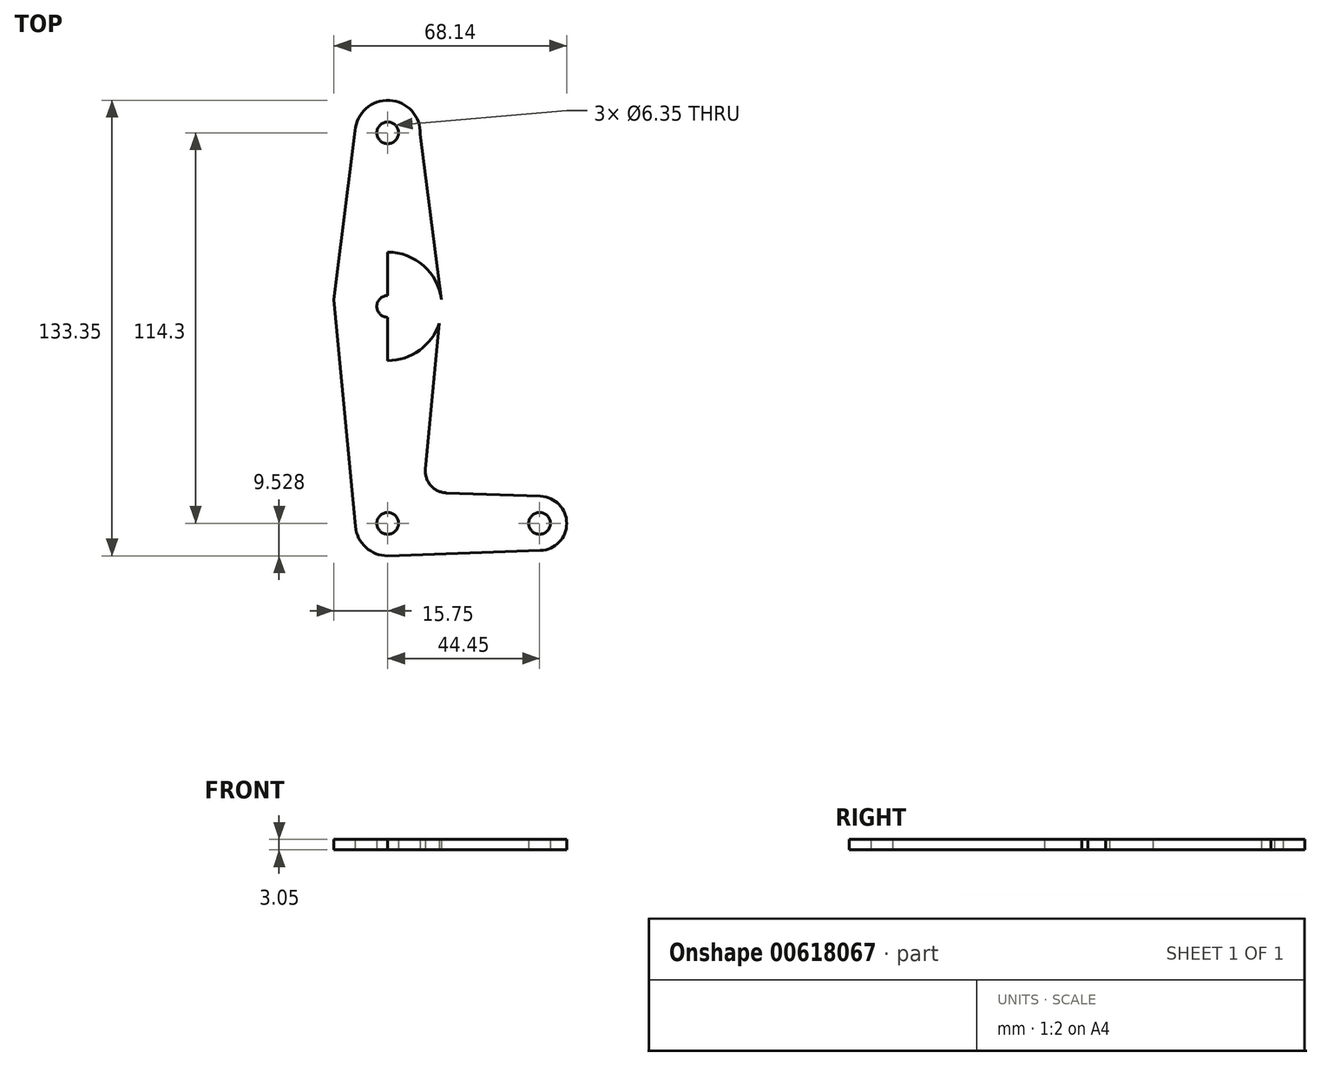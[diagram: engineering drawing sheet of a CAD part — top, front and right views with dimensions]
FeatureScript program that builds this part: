
annotation { "Feature Type Name" : "Feature", "Feature Type Description" : "" }
export const myFeature = defineFeature(function(context is Context, id is Id, definition is map)
    precondition{}
    {
        {
            var Q0;
            Q0=qCreatedBy(makeId("Top.planeOp"),FACE);
            var sketch = newSketch(context, id + "F0", { "sketchPlane" : qUnion([Q0])});
            skLineSegment(sketch, "E0", {"start": v(0, 86.7) * mm, "end": v(0, -27.6) * mm});
            skLineSegment(sketch, "E1", {"start": v(0, -27.6) * mm, "end": v(44.45, -27.6) * mm});
            skCircle(sketch, "E2", {"center": v(0, 86.7) * mm, "radius": 9.53 * mm});
            skCircle(sketch, "E3", {"center": v(0, 35.9) * mm, "radius": 15.88 * mm});
            skCircle(sketch, "E4", {"center": v(0, -27.6) * mm, "radius": 9.53 * mm});
            skCircle(sketch, "E5", {"center": v(44.45, -27.6) * mm, "radius": 7.94 * mm});
            skLineSegment(sketch, "E6", {"start": v(9.52, 86.33) * mm, "end": v(15.75, 37.93) * mm});
            skLineSegment(sketch, "E7", {"start": v(15.75, 37.93) * mm, "end": v(11.06, -11.74) * mm});
            skLineSegment(sketch, "E8", {"start": v(-9.5, 87.31) * mm, "end": v(-15.75, 37.9) * mm});
            skLineSegment(sketch, "E9", {"start": v(-15.75, 37.9) * mm, "end": v(-9.48, -28.49) * mm});
            skLineSegment(sketch, "E10", {"start": v(17.16, -18.68) * mm, "end": v(44.73, -19.66) * mm});
            skLineSegment(sketch, "E11", {"start": v(0, -37.12) * mm, "end": v(44.73, -35.52) * mm});
            skArc(sketch, "E12.filletArc", {"start": v(11.06, -11.74) * mm, "mid": v(12.61, -16.52) * mm, "end": v(17.16, -18.68) * mm});
            skCircle(sketch, "E13", {"center": v(0, 86.7) * mm, "radius": 3.18 * mm});
            skCircle(sketch, "E14", {"center": v(0, 35.9) * mm, "radius": 3.18 * mm});
            skCircle(sketch, "E15", {"center": v(0, -27.6) * mm, "radius": 3.18 * mm});
            skCircle(sketch, "E16", {"center": v(44.45, -27.6) * mm, "radius": 3.18 * mm});
            skSolve(sketch);
        }
        {
            var Q0;
            {var subQ5=sQuery(id+"F0.wireOp",EDGE,"E8");Q0=makeQuery(id+"F0.imprint","IMPRINT",FACE,{"disambiguationData":[TD([[makeQuery(id+"F0.imprint","IMPRINT",EDGE,{"derivedFrom":subQ5}),1.0]])]});}
            var Q1;
            {var subQ5=sQuery(id+"F0.wireOp",EDGE,"E6");Q1=makeQuery(id+"F0.imprint","IMPRINT",FACE,{"disambiguationData":[TD([[makeQuery(id+"F0.imprint","IMPRINT",EDGE,{"derivedFrom":subQ5}),-1.0]])]});}
            var Q2;
            {var subQ0=sQuery(id+"F0.wireOp",EDGE,"E3");var subQ1=sQuery(id+"F0.wireOp",EDGE,"E0");var subQ2=makeQuery(id+"F0.imprint","INTERSECT",VERTEX,{"disambiguationData":[OD(1.0)],"derivedFrom":[subQ1,subQ0]});Q2=makeQuery(id+"F0.imprint","IMPRINT",FACE,{"disambiguationData":[TD([[makeQuery(id+"F0.imprint","IMPRINT",EDGE,{"disambiguationData":[TD([[subQ2,-1.0]])],"derivedFrom":subQ1}),-1.0]])]});}
            var Q3;
            {var subQ11=sQuery(id+"F0.wireOp",EDGE,"E10");Q3=makeQuery(id+"F0.imprint","IMPRINT",FACE,{"disambiguationData":[TD([[makeQuery(id+"F0.imprint","IMPRINT",EDGE,{"derivedFrom":subQ11}),-1.0]])]});}
            var Q4;
            {var subQ0=sQuery(id+"F0.wireOp",EDGE,"E5");var subQ1=sQuery(id+"F0.wireOp",EDGE,"E1");var subQ2=makeQuery(id+"F0.imprint","INTERSECT",VERTEX,{"derivedFrom":[subQ1,subQ0]});Q4=makeQuery(id+"F0.imprint","IMPRINT",FACE,{"disambiguationData":[TD([[makeQuery(id+"F0.imprint","IMPRINT",EDGE,{"disambiguationData":[TD([[subQ2,1.0]])],"derivedFrom":subQ1}),-1.0]])]});}
            var Q5;
            {var subQ1=sQuery(id+"F0.wireOp",EDGE,"E3");var subQ3=sQuery(id+"F0.wireOp",EDGE,"E0");var subQ9=makeQuery(id+"F0.imprint","INTERSECT",VERTEX,{"disambiguationData":[OD(0.0)],"derivedFrom":[subQ3,subQ1]});Q5=makeQuery(id+"F0.imprint","IMPRINT",FACE,{"disambiguationData":[TD([[makeQuery(id+"F0.imprint","IMPRINT",EDGE,{"disambiguationData":[TD([[subQ9,-1.0]])],"derivedFrom":subQ3}),1.0]])]});}
            var Q6;
            {var subQ1=sQuery(id+"F0.wireOp",EDGE,"E3");var subQ3=sQuery(id+"F0.wireOp",EDGE,"E0");var subQ4=makeQuery(id+"F0.imprint","INTERSECT",VERTEX,{"disambiguationData":[OD(0.0)],"derivedFrom":[subQ3,subQ1]});Q6=makeQuery(id+"F0.imprint","IMPRINT",FACE,{"disambiguationData":[TD([[makeQuery(id+"F0.imprint","IMPRINT",EDGE,{"disambiguationData":[TD([[subQ4,-1.0]])],"derivedFrom":subQ3}),-1.0]])]});}
            var Q7;
            Q7=makeQuery(id+"F0.imprint","IMPRINT",FACE,{"disambiguationData":[TD([[makeQuery(id+"F0.imprint","IMPRINT",EDGE,{"derivedFrom":sQuery(id+"F0.wireOp",EDGE,"E13")}),-1.0]])]});
            var Q8;
            {var subQ0=sQuery(id+"F0.wireOp",EDGE,"E4");var subQ8=sQuery(id+"F0.wireOp",EDGE,"E0");var subQ10=makeQuery(id+"F0.imprint","INTERSECT",VERTEX,{"derivedFrom":[subQ8,subQ0]});Q8=makeQuery(id+"F0.imprint","IMPRINT",FACE,{"disambiguationData":[TD([[makeQuery(id+"F0.imprint","IMPRINT",EDGE,{"disambiguationData":[TD([[subQ10,-1.0]])],"derivedFrom":subQ8}),-1.0]])]});}
            var Q9;
            {var subQ0=sQuery(id+"F0.wireOp",EDGE,"E4");var subQ1=sQuery(id+"F0.wireOp",EDGE,"E0");var subQ2=makeQuery(id+"F0.imprint","INTERSECT",VERTEX,{"derivedFrom":[subQ1,subQ0]});Q9=makeQuery(id+"F0.imprint","IMPRINT",FACE,{"disambiguationData":[TD([[makeQuery(id+"F0.imprint","IMPRINT",EDGE,{"disambiguationData":[TD([[subQ2,-1.0]])],"derivedFrom":subQ1}),1.0]])]});}
            var Q10;
            Q10=makeQuery(id+"F0.imprint","IMPRINT",FACE,{"disambiguationData":[TD([[makeQuery(id+"F0.imprint","IMPRINT",EDGE,{"derivedFrom":sQuery(id+"F0.wireOp",EDGE,"E16")}),-1.0]])]});
            extrude(context, id + "F1", {"entities" : qUnion([Q0, Q1, Q2, Q3, Q4, Q5, Q6, Q7, Q8, Q9, Q10]), "depth" : 3.05 * mm, "offsetDistance" : 25.4 * mm});
        }
    });
